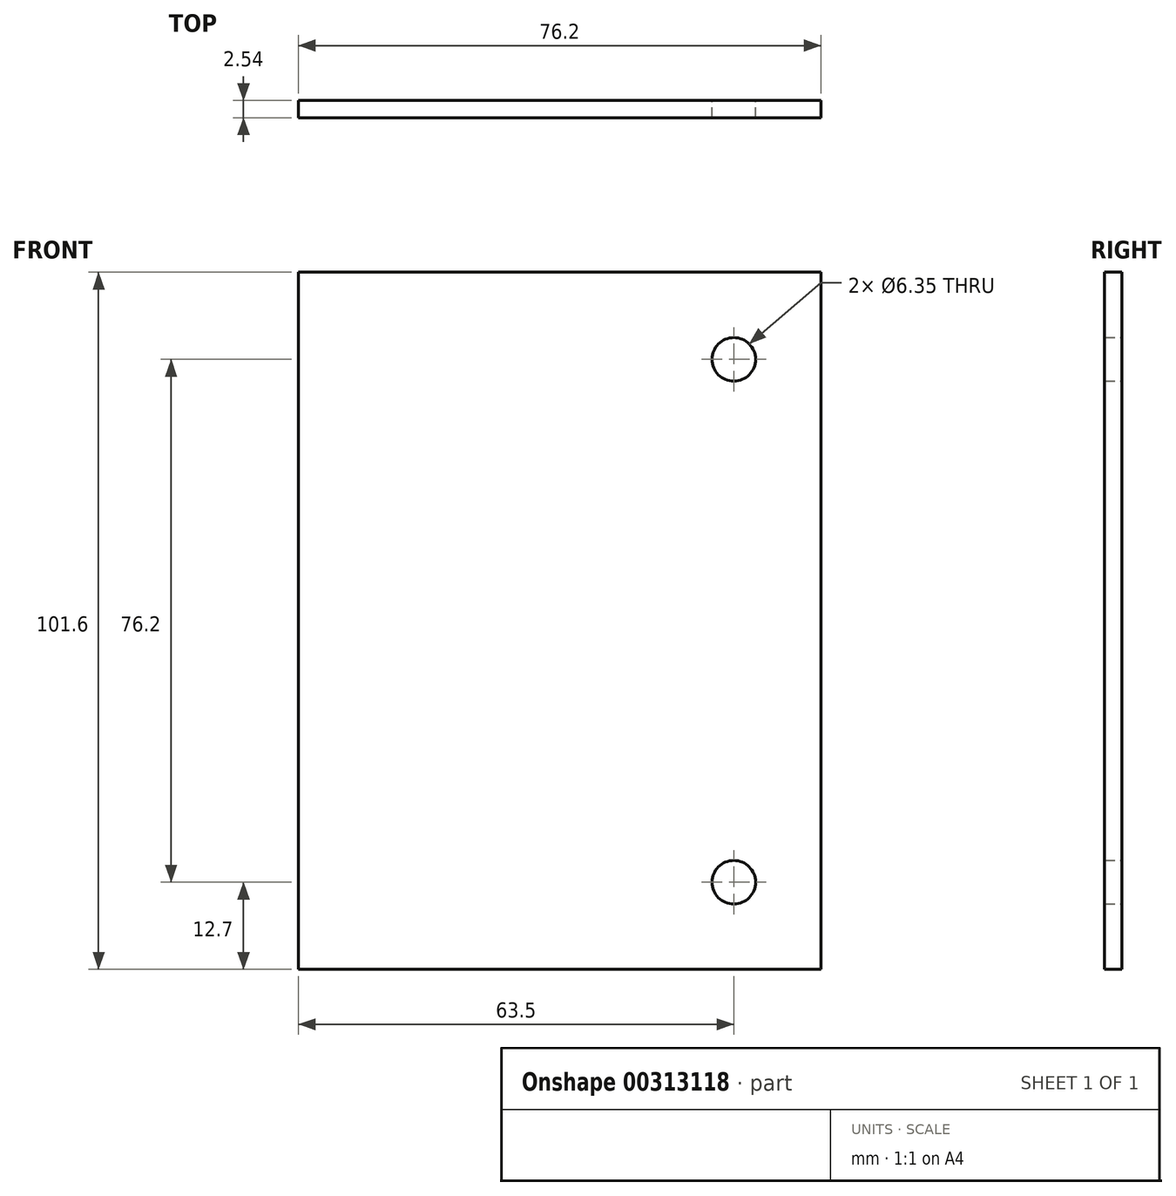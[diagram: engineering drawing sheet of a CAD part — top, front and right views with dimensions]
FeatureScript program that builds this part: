
annotation { "Feature Type Name" : "Feature", "Feature Type Description" : "" }
export const myFeature = defineFeature(function(context is Context, id is Id, definition is map)
    precondition{}
    {
        {
            var Q0;
            Q0=qCreatedBy(makeId("Front.planeOp"),FACE);
            var sketch = newSketch(context, id + "F0", { "sketchPlane" : qUnion([Q0])});
            skLineSegment(sketch, "E0.bottom", {"start": v(38.1, 50.8) * mm, "end": v(-38.1, 50.8) * mm});
            skLineSegment(sketch, "E0.top", {"start": v(38.1, -50.8) * mm, "end": v(-38.1, -50.8) * mm});
            skLineSegment(sketch, "E0.left", {"start": v(38.1, 50.8) * mm, "end": v(38.1, -50.8) * mm});
            skLineSegment(sketch, "E0.right", {"start": v(-38.1, 50.8) * mm, "end": v(-38.1, -50.8) * mm});
            skPoint(sketch, "E0.middle", {"position": v(0, 0) * mm});
            skCircle(sketch, "E1", {"center": v(25.4, 38.1) * mm, "radius": 3.18 * mm});
            skCircle(sketch, "E2", {"center": v(25.4, -38.1) * mm, "radius": 3.18 * mm});
            skSolve(sketch);
        }
        {
            var Q0;
            Q0 = qSketchRegion(id + "F0", true);
            extrude(context, id + "F1", {"entities" : qUnion([Q0]), "endBound" : BoundingType.SYMMETRIC, "depth" : 2.54 * mm});
        }
    });
